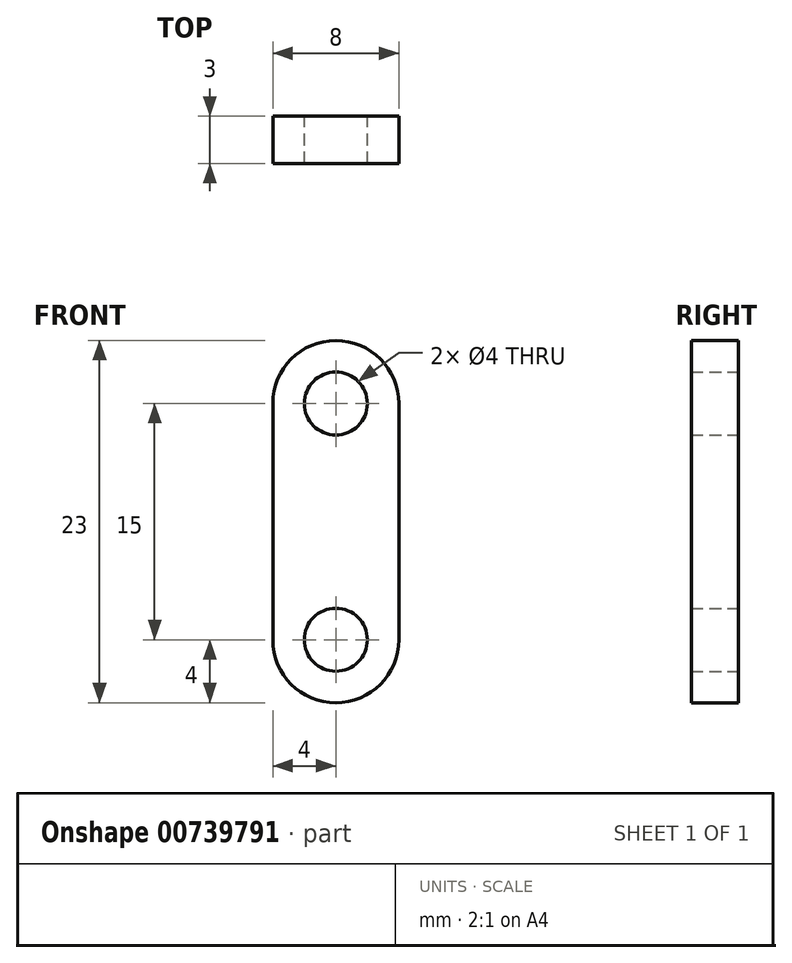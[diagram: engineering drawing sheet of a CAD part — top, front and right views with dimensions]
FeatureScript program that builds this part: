
annotation { "Feature Type Name" : "Feature", "Feature Type Description" : "" }
export const myFeature = defineFeature(function(context is Context, id is Id, definition is map)
    precondition{}
    {
        {
            var Q0;
            Q0=qCreatedBy(makeId("Front.planeOp"),FACE);
            var sketch = newSketch(context, id + "F0", { "sketchPlane" : qUnion([Q0])});
            skLineSegment(sketch, "E0.bottom", {"start": v(4, 7.5) * mm, "end": v(-4, 7.5) * mm, "construction": true});
            skLineSegment(sketch, "E0.top", {"start": v(4, -7.5) * mm, "end": v(-4, -7.5) * mm, "construction": true});
            skLineSegment(sketch, "E0.left", {"start": v(4, 7.5) * mm, "end": v(4, -7.5) * mm});
            skLineSegment(sketch, "E0.right", {"start": v(-4, 7.5) * mm, "end": v(-4, -7.5) * mm});
            skPoint(sketch, "E0.middle", {"position": v(0, 0) * mm});
            skArc(sketch, "E1", {"start": v(4, 7.5) * mm, "mid": v(0, 11.5) * mm, "end": v(-4, 7.5) * mm});
            skArc(sketch, "E2", {"start": v(-4, -7.5) * mm, "mid": v(0, -11.5) * mm, "end": v(4, -7.5) * mm});
            skCircle(sketch, "E3", {"center": v(0, 7.5) * mm, "radius": 2 * mm});
            skCircle(sketch, "E4", {"center": v(0, -7.5) * mm, "radius": 2 * mm});
            skSolve(sketch);
        }
        {
            var Q0;
            Q0=makeQuery(id+"F0.imprint","IMPRINT",FACE,{"disambiguationData":[TD([[makeQuery(id+"F0.imprint","IMPRINT",EDGE,{"derivedFrom":sQuery(id+"F0.wireOp",EDGE,"E0.left")}),-1.0]])]});
            extrude(context, id + "F1", {"entities" : qUnion([Q0]), "depth" : 3 * mm, "offsetDistance" : 25 * mm});
        }
    });
